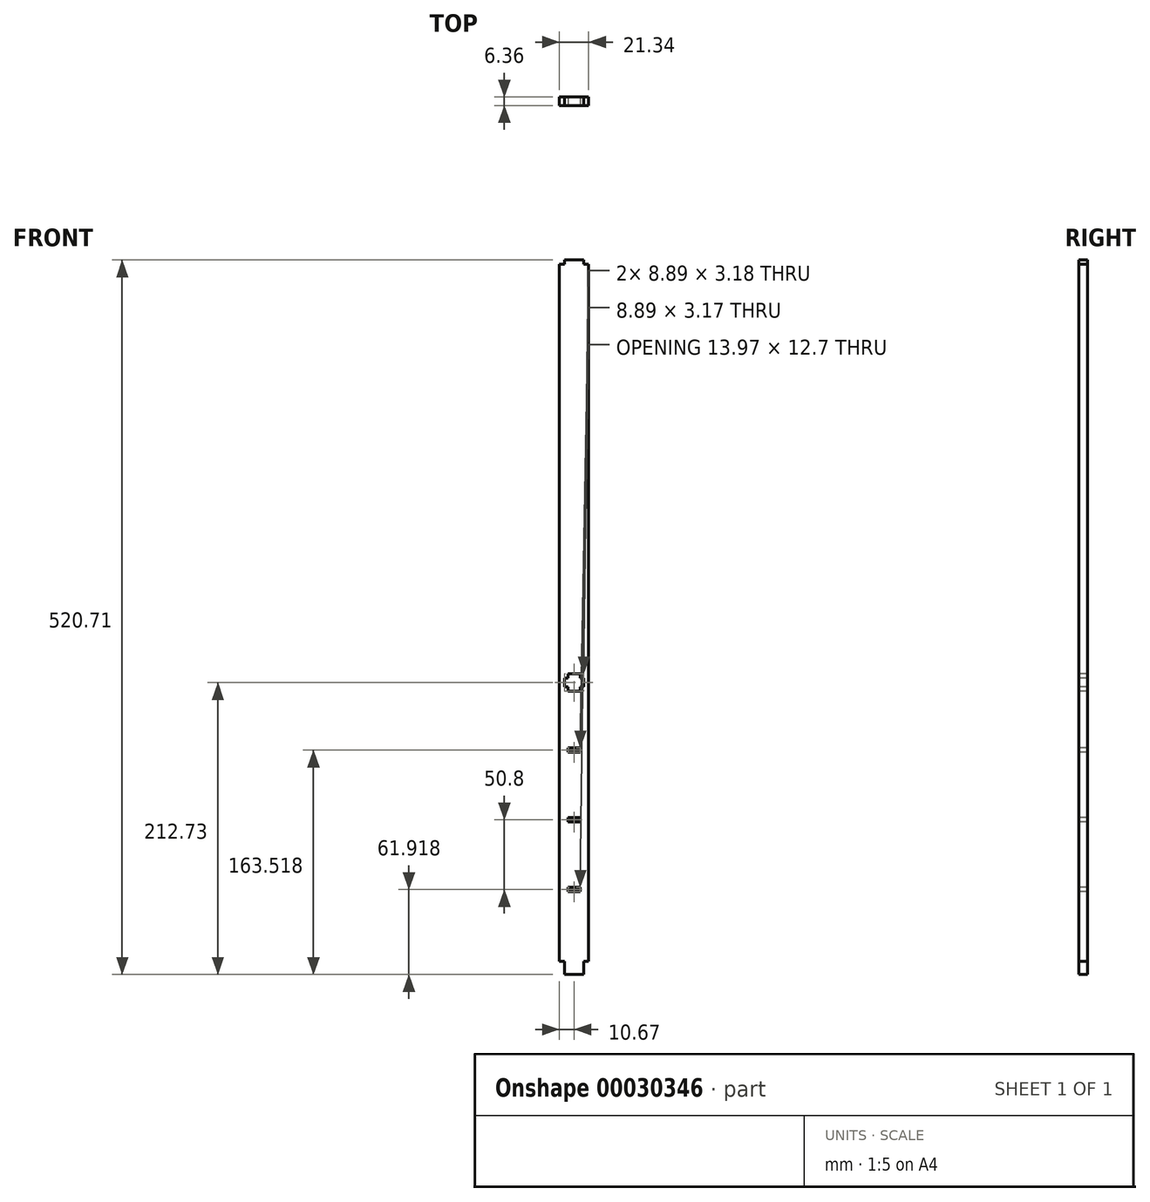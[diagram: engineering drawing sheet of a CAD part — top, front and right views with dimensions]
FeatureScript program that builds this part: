
annotation { "Feature Type Name" : "Feature", "Feature Type Description" : "" }
export const myFeature = defineFeature(function(context is Context, id is Id, definition is map)
    precondition{}
    {
        {
            var Q0;
            Q0=qCreatedBy(makeId("Front.planeOp"),FACE);
            var sketch = newSketch(context, id + "F0", { "sketchPlane" : qUnion([Q0])});
            skLineSegment(sketch, "E0", {"start": v(-10.67, 0) * mm, "end": v(-10.67, 508) * mm});
            skLineSegment(sketch, "E1", {"start": v(-10.67, 508) * mm, "end": v(10.67, 508) * mm});
            skLineSegment(sketch, "E2", {"start": v(10.67, 508) * mm, "end": v(10.67, 0) * mm});
            skLineSegment(sketch, "E3", {"start": v(10.67, 0) * mm, "end": v(6.99, 0) * mm});
            skLineSegment(sketch, "E4", {"start": v(6.99, 0) * mm, "end": v(6.99, -9.52) * mm});
            skLineSegment(sketch, "E5", {"start": v(6.99, -9.52) * mm, "end": v(-6.99, -9.52) * mm});
            skLineSegment(sketch, "E6", {"start": v(-6.99, -9.52) * mm, "end": v(-6.99, 0) * mm});
            skLineSegment(sketch, "E7", {"start": v(-6.99, 0) * mm, "end": v(-10.67, 0) * mm});
            skSolve(sketch);
        }
        {
            var Q0;
            Q0 = qSketchRegion(id + "F0", true);
            extrude(context, id + "F1", {"entities" : qUnion([Q0]), "endBound" : BoundingType.SYMMETRIC, "depth" : 6.35 * mm});
        }
        {
            var Q0;
            Q0=qCreatedBy(makeId("Front.planeOp"),FACE);
            var sketch = newSketch(context, id + "F2", { "sketchPlane" : qUnion([Q0])});
            skLineSegment(sketch, "E8.bottom", {"start": v(-6.99, 508) * mm, "end": v(6.99, 508) * mm});
            skLineSegment(sketch, "E8.top", {"start": v(-6.99, 511.18) * mm, "end": v(6.99, 511.18) * mm});
            skLineSegment(sketch, "E8.left", {"start": v(-6.98, 508) * mm, "end": v(-6.99, 511.18) * mm});
            skLineSegment(sketch, "E8.right", {"start": v(6.99, 508) * mm, "end": v(6.99, 511.18) * mm});
            skSolve(sketch);
        }
        {
            var Q0;
            Q0 = qSketchRegion(id + "F2", true);
            var Q1;
            Q1=makeQuery(id+"F1.opExtrude","CAP_FACE",FACE,{"disambiguationData":[OSD([sQuery(id+"F0.wireOp",EDGE,"E0"),sQuery(id+"F0.wireOp",EDGE,"E1"),sQuery(id+"F0.wireOp",EDGE,"E2"),sQuery(id+"F0.wireOp",EDGE,"E3"),sQuery(id+"F0.wireOp",EDGE,"E4"),sQuery(id+"F0.wireOp",EDGE,"E5"),sQuery(id+"F0.wireOp",EDGE,"E6"),sQuery(id+"F0.wireOp",EDGE,"E7")])],"isStart":false});
            var Q2;
            Q2=makeQuery(id+"F1.opExtrude","CAP_FACE",FACE,{"disambiguationData":[OSD([sQuery(id+"F0.wireOp",EDGE,"E0"),sQuery(id+"F0.wireOp",EDGE,"E1"),sQuery(id+"F0.wireOp",EDGE,"E2"),sQuery(id+"F0.wireOp",EDGE,"E3"),sQuery(id+"F0.wireOp",EDGE,"E4"),sQuery(id+"F0.wireOp",EDGE,"E5"),sQuery(id+"F0.wireOp",EDGE,"E6"),sQuery(id+"F0.wireOp",EDGE,"E7")])],"isStart":true});
            extrude(context, id + "F3", {"entities" : qUnion([Q0]), "operationType" : NewBodyOperationType.ADD, "endBound" : BoundingType.UP_TO_SURFACE, "endBoundEntityFace" : qUnion([Q1]), "depth" : 25.4 * mm, "hasSecondDirection" : true, "secondDirectionBound" : SecondDirectionBoundingType.UP_TO_SURFACE, "secondDirectionOppositeDirection" : true, "secondDirectionBoundEntityFace" : qUnion([Q2]), "secondDirectionDepth" : 25.4 * mm});
        }
        {
            var Q0;
            Q0=makeQuery(id+"F3.boolean.opBoolean","MERGE",FACE,{"derivedFrom":[makeQuery(id+"F1.opExtrude","CAP_FACE",FACE,{"disambiguationData":[OSD([sQuery(id+"F0.wireOp",EDGE,"E0"),sQuery(id+"F0.wireOp",EDGE,"E1"),sQuery(id+"F0.wireOp",EDGE,"E2"),sQuery(id+"F0.wireOp",EDGE,"E3"),sQuery(id+"F0.wireOp",EDGE,"E4"),sQuery(id+"F0.wireOp",EDGE,"E5"),sQuery(id+"F0.wireOp",EDGE,"E6"),sQuery(id+"F0.wireOp",EDGE,"E7")])],"isStart":false}),makeQuery(id+"F3.opExtrude","CAP_FACE",FACE,{"disambiguationData":[OSD([sQuery(id+"F2.wireOp",EDGE,"E8.bottom"),sQuery(id+"F2.wireOp",EDGE,"E8.top"),sQuery(id+"F2.wireOp",EDGE,"E8.left"),sQuery(id+"F2.wireOp",EDGE,"E8.right")])],"isStart":false})]});
            var sketch = newSketch(context, id + "F4", { "sketchPlane" : qUnion([Q0])});
            skLineSegment(sketch, "E9.bottom", {"start": v(-6.98, 206.38) * mm, "end": v(6.99, 206.38) * mm});
            skLineSegment(sketch, "E9.top", {"start": v(-6.98, 200.03) * mm, "end": v(6.99, 200.03) * mm});
            skLineSegment(sketch, "E9.left", {"start": v(-6.98, 206.38) * mm, "end": v(-6.98, 200.03) * mm});
            skLineSegment(sketch, "E9.right", {"start": v(6.99, 206.38) * mm, "end": v(6.99, 200.03) * mm});
            skPoint(sketch, "E10", {"position": v(6.99, 203.2) * mm});
            skSolve(sketch);
        }
        {
            var Q0;
            Q0 = qSketchRegion(id + "F4", true);
            extrude(context, id + "F5", {"entities" : qUnion([Q0]), "operationType" : NewBodyOperationType.REMOVE, "endBound" : BoundingType.UP_TO_NEXT, "oppositeDirection" : true, "depth" : 25.4 * mm});
        }
        {
            var Q0;
            Q0=makeQuery(id+"F3.boolean.opBoolean","MERGE",FACE,{"derivedFrom":[makeQuery(id+"F1.opExtrude","CAP_FACE",FACE,{"disambiguationData":[OSD([sQuery(id+"F0.wireOp",EDGE,"E0"),sQuery(id+"F0.wireOp",EDGE,"E1"),sQuery(id+"F0.wireOp",EDGE,"E2"),sQuery(id+"F0.wireOp",EDGE,"E3"),sQuery(id+"F0.wireOp",EDGE,"E4"),sQuery(id+"F0.wireOp",EDGE,"E5"),sQuery(id+"F0.wireOp",EDGE,"E6"),sQuery(id+"F0.wireOp",EDGE,"E7")])],"isStart":false}),makeQuery(id+"F3.opExtrude","CAP_FACE",FACE,{"disambiguationData":[OSD([sQuery(id+"F2.wireOp",EDGE,"E8.bottom"),sQuery(id+"F2.wireOp",EDGE,"E8.top"),sQuery(id+"F2.wireOp",EDGE,"E8.left"),sQuery(id+"F2.wireOp",EDGE,"E8.right")])],"isStart":false})]});
            var sketch = newSketch(context, id + "F6", { "sketchPlane" : qUnion([Q0])});
            skLineSegment(sketch, "E11.bottom", {"start": v(-4.45, 206.38) * mm, "end": v(4.45, 206.38) * mm});
            skLineSegment(sketch, "E11.top", {"start": v(-4.45, 209.55) * mm, "end": v(4.45, 209.55) * mm});
            skLineSegment(sketch, "E11.left", {"start": v(-4.45, 206.38) * mm, "end": v(-4.44, 209.55) * mm});
            skLineSegment(sketch, "E11.right", {"start": v(4.45, 206.38) * mm, "end": v(4.45, 209.55) * mm});
            skLineSegment(sketch, "E12.bottom", {"start": v(-4.45, 200.03) * mm, "end": v(4.45, 200.03) * mm});
            skLineSegment(sketch, "E12.top", {"start": v(-4.45, 196.85) * mm, "end": v(4.45, 196.85) * mm});
            skLineSegment(sketch, "E12.left", {"start": v(-4.45, 200.03) * mm, "end": v(-4.45, 196.85) * mm});
            skLineSegment(sketch, "E12.right", {"start": v(4.45, 200.03) * mm, "end": v(4.45, 196.85) * mm});
            skSolve(sketch);
        }
        {
            var Q0;
            Q0 = qSketchRegion(id + "F6", true);
            extrude(context, id + "F7", {"entities" : qUnion([Q0]), "operationType" : NewBodyOperationType.REMOVE, "endBound" : BoundingType.UP_TO_NEXT, "oppositeDirection" : true, "depth" : 25.4 * mm});
        }
        {
            var Q0;
            Q0=makeQuery(id+"F3.boolean.opBoolean","MERGE",FACE,{"derivedFrom":[makeQuery(id+"F1.opExtrude","CAP_FACE",FACE,{"disambiguationData":[OSD([sQuery(id+"F0.wireOp",EDGE,"E0"),sQuery(id+"F0.wireOp",EDGE,"E1"),sQuery(id+"F0.wireOp",EDGE,"E2"),sQuery(id+"F0.wireOp",EDGE,"E3"),sQuery(id+"F0.wireOp",EDGE,"E4"),sQuery(id+"F0.wireOp",EDGE,"E5"),sQuery(id+"F0.wireOp",EDGE,"E6"),sQuery(id+"F0.wireOp",EDGE,"E7")])],"isStart":false}),makeQuery(id+"F3.opExtrude","CAP_FACE",FACE,{"disambiguationData":[OSD([sQuery(id+"F2.wireOp",EDGE,"E8.bottom"),sQuery(id+"F2.wireOp",EDGE,"E8.top"),sQuery(id+"F2.wireOp",EDGE,"E8.left"),sQuery(id+"F2.wireOp",EDGE,"E8.right")])],"isStart":false})]});
            var sketch = newSketch(context, id + "F8", { "sketchPlane" : qUnion([Q0])});
            skLineSegment(sketch, "E13.bottom", {"start": v(-4.45, 53.98) * mm, "end": v(4.45, 53.98) * mm});
            skLineSegment(sketch, "E13.top", {"start": v(-4.44, 50.8) * mm, "end": v(4.45, 50.8) * mm});
            skLineSegment(sketch, "E13.left", {"start": v(-4.45, 53.98) * mm, "end": v(-4.45, 50.8) * mm});
            skLineSegment(sketch, "E13.right", {"start": v(4.45, 53.98) * mm, "end": v(4.45, 50.8) * mm});
            skLineSegment(sketch, "E14.bottom", {"start": v(-4.45, 104.78) * mm, "end": v(4.45, 104.78) * mm});
            skLineSegment(sketch, "E14.top", {"start": v(-4.44, 101.6) * mm, "end": v(4.44, 101.6) * mm});
            skLineSegment(sketch, "E14.left", {"start": v(-4.45, 104.78) * mm, "end": v(-4.45, 101.6) * mm});
            skLineSegment(sketch, "E14.right", {"start": v(4.44, 104.78) * mm, "end": v(4.44, 101.6) * mm});
            skLineSegment(sketch, "E15.bottom", {"start": v(-4.44, 155.58) * mm, "end": v(4.44, 155.58) * mm});
            skLineSegment(sketch, "E15.top", {"start": v(-4.44, 152.4) * mm, "end": v(4.44, 152.4) * mm});
            skLineSegment(sketch, "E15.left", {"start": v(-4.45, 155.58) * mm, "end": v(-4.45, 152.4) * mm});
            skLineSegment(sketch, "E15.right", {"start": v(4.44, 155.58) * mm, "end": v(4.44, 152.4) * mm});
            skSolve(sketch);
        }
        {
            var Q0;
            Q0 = qSketchRegion(id + "F8", true);
            extrude(context, id + "F9", {"entities" : qUnion([Q0]), "operationType" : NewBodyOperationType.REMOVE, "endBound" : BoundingType.UP_TO_NEXT, "oppositeDirection" : true, "depth" : 25.4 * mm});
        }
    });
